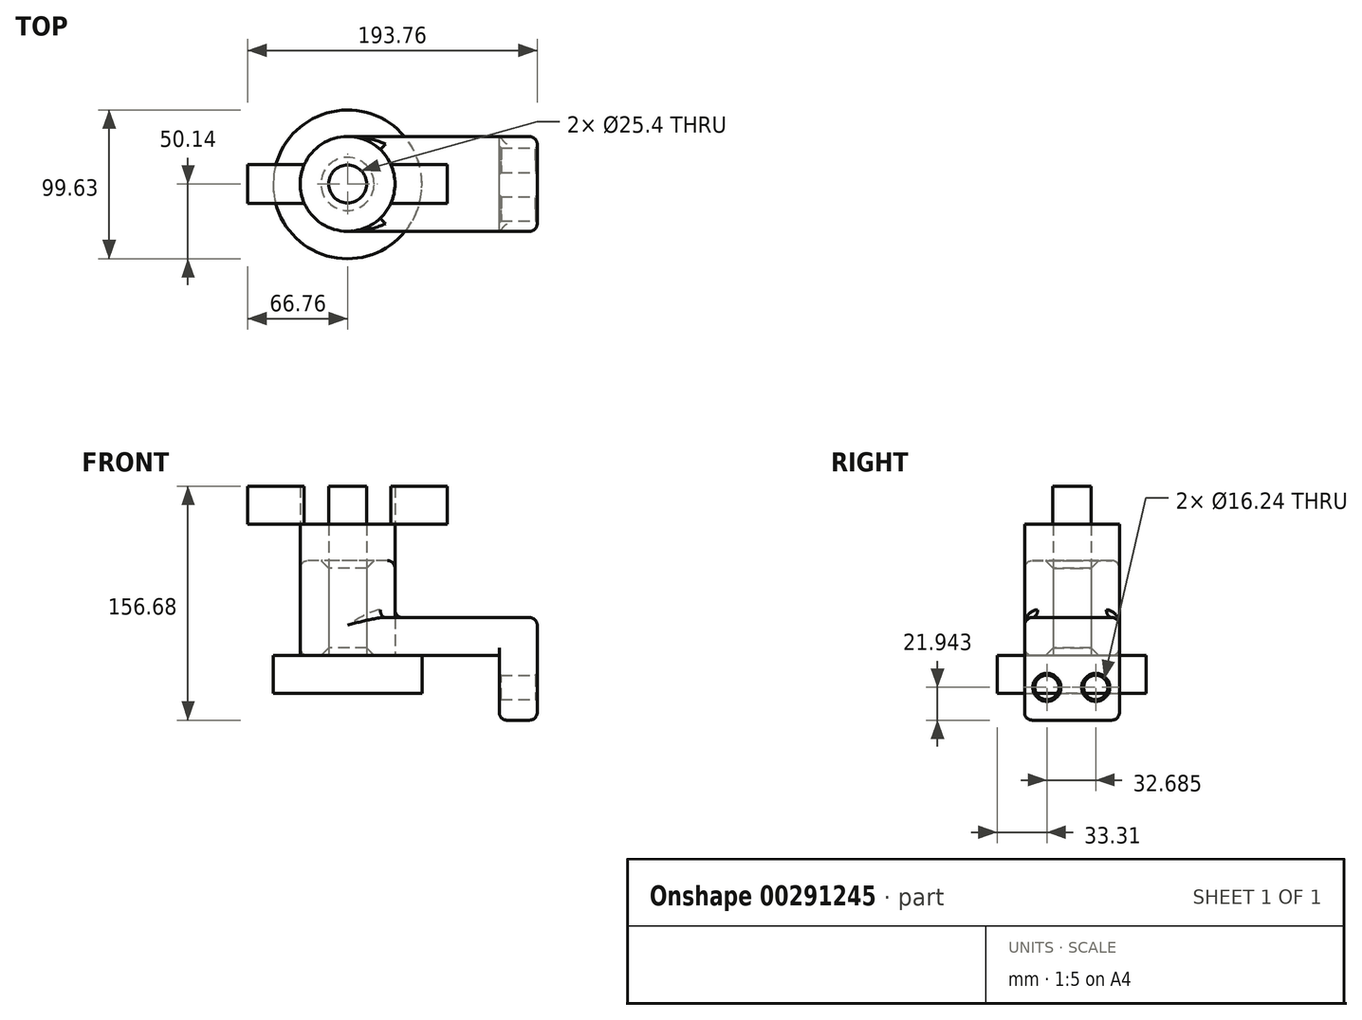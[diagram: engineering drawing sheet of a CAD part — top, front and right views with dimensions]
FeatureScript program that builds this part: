
annotation { "Feature Type Name" : "Feature", "Feature Type Description" : "" }
export const myFeature = defineFeature(function(context is Context, id is Id, definition is map)
    precondition{}
    {
        {
            var Q0;
            Q0=qCreatedBy(makeId("Top.planeOp"),FACE);
            var sketch = newSketch(context, id + "F0", { "sketchPlane" : qUnion([Q0])});
            skLineSegment(sketch, "E0.bottom", {"start": v(0, 0) * mm, "end": v(127, 0) * mm});
            skLineSegment(sketch, "E0.top", {"start": v(0, 63.5) * mm, "end": v(127, 63.5) * mm});
            skLineSegment(sketch, "E0.left", {"start": v(0, 0) * mm, "end": v(0, 63.5) * mm});
            skLineSegment(sketch, "E0.right", {"start": v(127, 0) * mm, "end": v(127, 63.5) * mm});
            skCircle(sketch, "E1", {"center": v(0, 31.75) * mm, "radius": 31.75 * mm});
            skCircle(sketch, "E2", {"center": v(0, 31.75) * mm, "radius": 12.7 * mm});
            skSolve(sketch);
        }
        {
            var Q0;
            Q0 = qSketchRegion(id + "F0", true);
            extrude(context, id + "F1", {"entities" : qUnion([Q0]), "depth" : 25.4 * mm});
        }
        {
            var Q0;
            {var subQ1=sQuery(id+"F0.wireOp",EDGE,"E0.left");var subQ3=sQuery(id+"F0.wireOp",EDGE,"E2");var subQ4=makeQuery(id+"F0.imprint","INTERSECT",VERTEX,{"disambiguationData":[OD(0.0)],"derivedFrom":[subQ1,subQ3]});Q0=makeQuery(id+"F0.imprint","IMPRINT",FACE,{"disambiguationData":[TD([[makeQuery(id+"F0.imprint","IMPRINT",EDGE,{"disambiguationData":[TD([[subQ4,1.0]])],"derivedFrom":subQ3}),-1.0]])]});}
            var Q1;
            {var subQ1=sQuery(id+"F0.wireOp",EDGE,"E0.left");var subQ3=sQuery(id+"F0.wireOp",EDGE,"E2");var subQ4=makeQuery(id+"F0.imprint","INTERSECT",VERTEX,{"disambiguationData":[OD(0.0)],"derivedFrom":[subQ1,subQ3]});Q1=makeQuery(id+"F0.imprint","IMPRINT",FACE,{"disambiguationData":[TD([[makeQuery(id+"F0.imprint","IMPRINT",EDGE,{"disambiguationData":[TD([[subQ4,-1.0]])],"derivedFrom":subQ3}),-1.0]])]});}
            extrude(context, id + "F2", {"entities" : qUnion([Q0, Q1]), "operationType" : NewBodyOperationType.ADD, "depth" : 63.5 * mm});
        }
        {
            var Q0;
            Q0=makeQuery(id+"F1.opExtrude","SWEPT_FACE",FACE,{"disambiguationData":[OSD([sQuery(id+"F0.wireOp",EDGE,"E0.right")])]});
            var sketch = newSketch(context, id + "F3", { "sketchPlane" : qUnion([Q0])});
            skLineSegment(sketch, "E3.bottom", {"start": v(0, 25.4) * mm, "end": v(63.5, 25.4) * mm});
            skLineSegment(sketch, "E3.top", {"start": v(0, -43.4) * mm, "end": v(63.5, -43.4) * mm});
            skLineSegment(sketch, "E3.left", {"start": v(0, 25.4) * mm, "end": v(0, -43.4) * mm});
            skLineSegment(sketch, "E3.right", {"start": v(63.5, 25.4) * mm, "end": v(63.5, -43.4) * mm});
            skSolve(sketch);
        }
        {
            var Q0;
            {var subQ0=sQuery(id+"F3.wireOp",EDGE,"E3.top");Q0=makeQuery(id+"F3.imprint","IMPRINT",FACE,{"disambiguationData":[TD([[makeQuery(id+"F3.imprint","IMPRINT",EDGE,{"derivedFrom":subQ0}),1.0]])]});}
            var sketch = newSketch(context, id + "F4", { "sketchPlane" : qUnion([Q0])});
            skLineSegment(sketch, "E4", {"start": v(31.26, 0) * mm, "end": v(31.26, -42.43) * mm, "construction": true});
            skCircle(sketch, "E5", {"center": v(14.92, -21.46) * mm, "radius": 8.12 * mm});
            skCircle(sketch, "E6.MirrorC", {"center": v(47.6, -21.46) * mm, "radius": 8.12 * mm});
            skSolve(sketch);
        }
        {
            var Q0;
            Q0=makeQuery(id+"F4.imprint","IMPRINT",FACE,{"disambiguationData":[TD([[makeQuery(id+"F4.imprint","IMPRINT",EDGE,{"derivedFrom":sQuery(id+"F4.wireOp",EDGE,"E5")}),-1.0]])]});
            extrude(context, id + "F5", {"entities" : qUnion([Q0]), "operationType" : NewBodyOperationType.ADD, "oppositeDirection" : true, "depth" : 25.4 * mm});
        }
        {
            var Q0;
            {var subQ0=sQuery(id+"F0.wireOp",EDGE,"E1");Q0=makeQuery(id+"F2.boolean.opBoolean","INTERSECT",EDGE,{"derivedFrom":[makeQuery(id+"F1.opExtrude","CAP_FACE",FACE,{"disambiguationData":[OSD([sQuery(id+"F0.wireOp",EDGE,"E0.bottom"),sQuery(id+"F0.wireOp",EDGE,"E0.top"),sQuery(id+"F0.wireOp",EDGE,"E0.right"),subQ0,sQuery(id+"F0.wireOp",EDGE,"E2")])],"isStart":false}),makeQuery(id+"F2.opExtrude","SWEPT_FACE",FACE,{"disambiguationData":[OSD([subQ0])]})]});}
            var Q1;
            Q1=makeQuery(id+"F1.opExtrude","CAP_EDGE",EDGE,{"disambiguationData":[OSD([sQuery(id+"F0.wireOp",EDGE,"E0.bottom")])],"isStart":false});
            var Q2;
            Q2=makeQuery(id+"F1.opExtrude","CAP_EDGE",EDGE,{"disambiguationData":[OSD([sQuery(id+"F0.wireOp",EDGE,"E0.top")])],"isStart":false});
            var Q3;
            Q3=makeQuery(id+"F5.opExtrude","CAP_EDGE",EDGE,{"disambiguationData":[OSD([sQuery(id+"F0.wireOp",EDGE,"E0.right")])],"isStart":false});
            var Q4;
            Q4=makeQuery(id+"F1.opExtrude","CAP_EDGE",EDGE,{"disambiguationData":[OSD([sQuery(id+"F0.wireOp",EDGE,"E0.right")])],"isStart":false});
            var Q5;
            Q5=makeQuery(id+"F1.opExtrude","CAP_EDGE",EDGE,{"disambiguationData":[OSD([sQuery(id+"F0.wireOp",EDGE,"E0.top")])],"isStart":true});
            var Q6;
            Q6=makeQuery(id+"F5.opExtrude","CAP_EDGE",EDGE,{"disambiguationData":[OSD([sQuery(id+"F3.wireOp",EDGE,"E3.top")])],"isStart":false});
            var Q7;
            Q7=makeQuery(id+"F5.opExtrude","SWEPT_EDGE",EDGE,{"disambiguationData":[OSD([sQuery(id+"F3.wireOp",EDGE,"E3.top"),sQuery(id+"F3.wireOp",EDGE,"E3.right")])]});
            var Q8;
            Q8=makeQuery(id+"F5.opExtrude","CAP_EDGE",EDGE,{"disambiguationData":[OSD([sQuery(id+"F3.wireOp",EDGE,"E3.top")])],"isStart":true});
            var Q9;
            Q9=makeQuery(id+"F5.opExtrude","SWEPT_EDGE",EDGE,{"disambiguationData":[OSD([sQuery(id+"F3.wireOp",EDGE,"E3.top"),sQuery(id+"F3.wireOp",EDGE,"E3.left")])]});
            var Q10;
            Q10=makeQuery(id+"F5.boolean.opBoolean","MERGE",EDGE,{"derivedFrom":[makeQuery(id+"F1.opExtrude","SWEPT_EDGE",EDGE,{"disambiguationData":[OSD([sQuery(id+"F0.wireOp",EDGE,"E0.top"),sQuery(id+"F0.wireOp",EDGE,"E0.right")])]}),makeQuery(id+"F5.opExtrude","CAP_EDGE",EDGE,{"disambiguationData":[OSD([sQuery(id+"F3.wireOp",EDGE,"E3.right")])],"isStart":true})]});
            var Q11;
            Q11=makeQuery(id+"F5.boolean.opBoolean","MERGE",EDGE,{"derivedFrom":[makeQuery(id+"F1.opExtrude","SWEPT_EDGE",EDGE,{"disambiguationData":[OSD([sQuery(id+"F0.wireOp",EDGE,"E0.bottom"),sQuery(id+"F0.wireOp",EDGE,"E0.right")])]}),makeQuery(id+"F5.opExtrude","CAP_EDGE",EDGE,{"disambiguationData":[OSD([sQuery(id+"F3.wireOp",EDGE,"E3.left")])],"isStart":true})]});
            fillet(context, id + "F6", {"entities" : qUnion([Q0, Q1, Q2, Q3, Q4, Q5, Q6, Q7, Q8, Q9, Q10, Q11]), "radius" : 5.08 * mm, "tangentPropagation" : true, "allowEdgeOverflow" : false});
        }
        {
            var Q0;
            Q0=makeQuery(id+"F2.opExtrude","CAP_EDGE",EDGE,{"disambiguationData":[OSD([sQuery(id+"F0.wireOp",EDGE,"E2")])],"isStart":false});
            var Q1;
            Q1=makeQuery(id+"F1.opExtrude","CAP_EDGE",EDGE,{"disambiguationData":[OSD([sQuery(id+"F0.wireOp",EDGE,"E2")])],"isStart":true});
            chamfer(context, id + "F7", {"entities" : qUnion([Q0, Q1]), "width" : 5.08 * mm, "tangentPropagation" : true});
        }
        {
            var Q0;
            Q0=makeQuery(id+"F2.opExtrude","CAP_EDGE",EDGE,{"disambiguationData":[OSD([sQuery(id+"F0.wireOp",EDGE,"E1")])],"isStart":false});
            fillet(context, id + "F8", {"entities" : qUnion([Q0]), "radius" : 5.08 * mm, "tangentPropagation" : true, "allowEdgeOverflow" : false});
        }
        {
            var Q0;
            Q0=makeQuery(id+"F5.opExtrude","CAP_EDGE",EDGE,{"disambiguationData":[OSD([sQuery(id+"F4.wireOp",EDGE,"E5")])],"isStart":true});
            var Q1;
            Q1=makeQuery(id+"F5.opExtrude","CAP_EDGE",EDGE,{"disambiguationData":[OSD([sQuery(id+"F4.wireOp",EDGE,"E6.MirrorC")])],"isStart":true});
            var Q2;
            Q2=makeQuery(id+"F5.opExtrude","CAP_EDGE",EDGE,{"disambiguationData":[OSD([sQuery(id+"F4.wireOp",EDGE,"E6.MirrorC")])],"isStart":false});
            var Q3;
            Q3=makeQuery(id+"F5.opExtrude","CAP_EDGE",EDGE,{"disambiguationData":[OSD([sQuery(id+"F4.wireOp",EDGE,"E5")])],"isStart":false});
            chamfer(context, id + "F9", {"entities" : qUnion([Q0, Q1, Q2, Q3]), "width" : 1.27 * mm, "tangentPropagation" : true});
        }
        {
            var Q0;
            {var subQ0=sQuery(id+"F0.wireOp",EDGE,"E2");var subQ1=sQuery(id+"F0.wireOp",EDGE,"E0.left");var subQ2=makeQuery(id+"F0.imprint","INTERSECT",VERTEX,{"disambiguationData":[OD(0.0)],"derivedFrom":[subQ1,subQ0]});Q0=makeQuery(id+"F0.imprint","IMPRINT",FACE,{"disambiguationData":[TD([[makeQuery(id+"F0.imprint","IMPRINT",EDGE,{"disambiguationData":[TD([[subQ2,-1.0]])],"derivedFrom":subQ1}),1.0]])]});}
            var Q1;
            {var subQ0=sQuery(id+"F0.wireOp",EDGE,"E2");var subQ1=sQuery(id+"F0.wireOp",EDGE,"E0.left");var subQ2=makeQuery(id+"F0.imprint","INTERSECT",VERTEX,{"disambiguationData":[OD(0.0)],"derivedFrom":[subQ1,subQ0]});Q1=makeQuery(id+"F0.imprint","IMPRINT",FACE,{"disambiguationData":[TD([[makeQuery(id+"F0.imprint","IMPRINT",EDGE,{"disambiguationData":[TD([[subQ2,-1.0]])],"derivedFrom":subQ1}),-1.0]])]});}
            extrude(context, id + "F10", {"entities" : qUnion([Q0, Q1]), "depth" : 87.88 * mm});
        }
        {
            var Q0;
            Q0=makeQuery(id+"F10.opExtrude","CAP_FACE",FACE,{"disambiguationData":[OSD([sQuery(id+"F0.wireOp",EDGE,"E2")])],"isStart":false});
            var sketch = newSketch(context, id + "F11", { "sketchPlane" : qUnion([Q0])});
            skLineSegment(sketch, "E7.bottom", {"start": v(-66.76, 44.67) * mm, "end": v(66.76, 44.67) * mm});
            skLineSegment(sketch, "E7.top", {"start": v(-66.76, 18.83) * mm, "end": v(66.76, 18.83) * mm});
            skLineSegment(sketch, "E7.left", {"start": v(-66.76, 44.67) * mm, "end": v(-66.76, 18.83) * mm});
            skLineSegment(sketch, "E7.right", {"start": v(66.76, 44.67) * mm, "end": v(66.76, 18.83) * mm});
            skPoint(sketch, "E7.middle", {"position": v(0, 31.75) * mm});
            skSolve(sketch);
        }
        {
            var Q0;
            Q0=makeQuery(id+"F11.imprint","IMPRINT",FACE,{"disambiguationData":[TD([[makeQuery(id+"F11.imprint","IMPRINT",EDGE,{"derivedFrom":sQuery(id+"F11.wireOp",EDGE,"E7.bottom")}),-1.0]])]});
            var Q1;
            Q1=makeQuery(id+"F11.imprint","IMPRINT",FACE,{"disambiguationData":[TD([[makeQuery(id+"F11.imprint","IMPRINT",EDGE,{"derivedFrom":makeQuery(id+"F10.opExtrude","CAP_EDGE",EDGE,{"disambiguationData":[OSD([sQuery(id+"F0.wireOp",EDGE,"E2")])],"isStart":false})}),1.0]])]});
            extrude(context, id + "F12", {"entities" : qUnion([Q0, Q1]), "operationType" : NewBodyOperationType.ADD, "depth" : 25.4 * mm});
        }
        {
            var Q0;
            {var subQ0=sQuery(id+"F0.wireOp",EDGE,"E2");var subQ1=sQuery(id+"F0.wireOp",EDGE,"E0.left");var subQ2=makeQuery(id+"F0.imprint","INTERSECT",VERTEX,{"disambiguationData":[OD(0.0)],"derivedFrom":[subQ1,subQ0]});Q0=makeQuery(id+"F0.imprint","IMPRINT",FACE,{"disambiguationData":[TD([[makeQuery(id+"F0.imprint","IMPRINT",EDGE,{"disambiguationData":[TD([[subQ2,-1.0]])],"derivedFrom":subQ1}),1.0]])]});}
            var sketch = newSketch(context, id + "F13", { "sketchPlane" : qUnion([Q0])});
            skCircle(sketch, "E8", {"center": v(0, 31.43) * mm, "radius": 49.82 * mm});
            skSolve(sketch);
        }
        {
            var Q0;
            Q0 = qSketchRegion(id + "F13", true);
            extrude(context, id + "F14", {"entities" : qUnion([Q0]), "oppositeDirection" : true, "depth" : 25.4 * mm});
        }
    });
